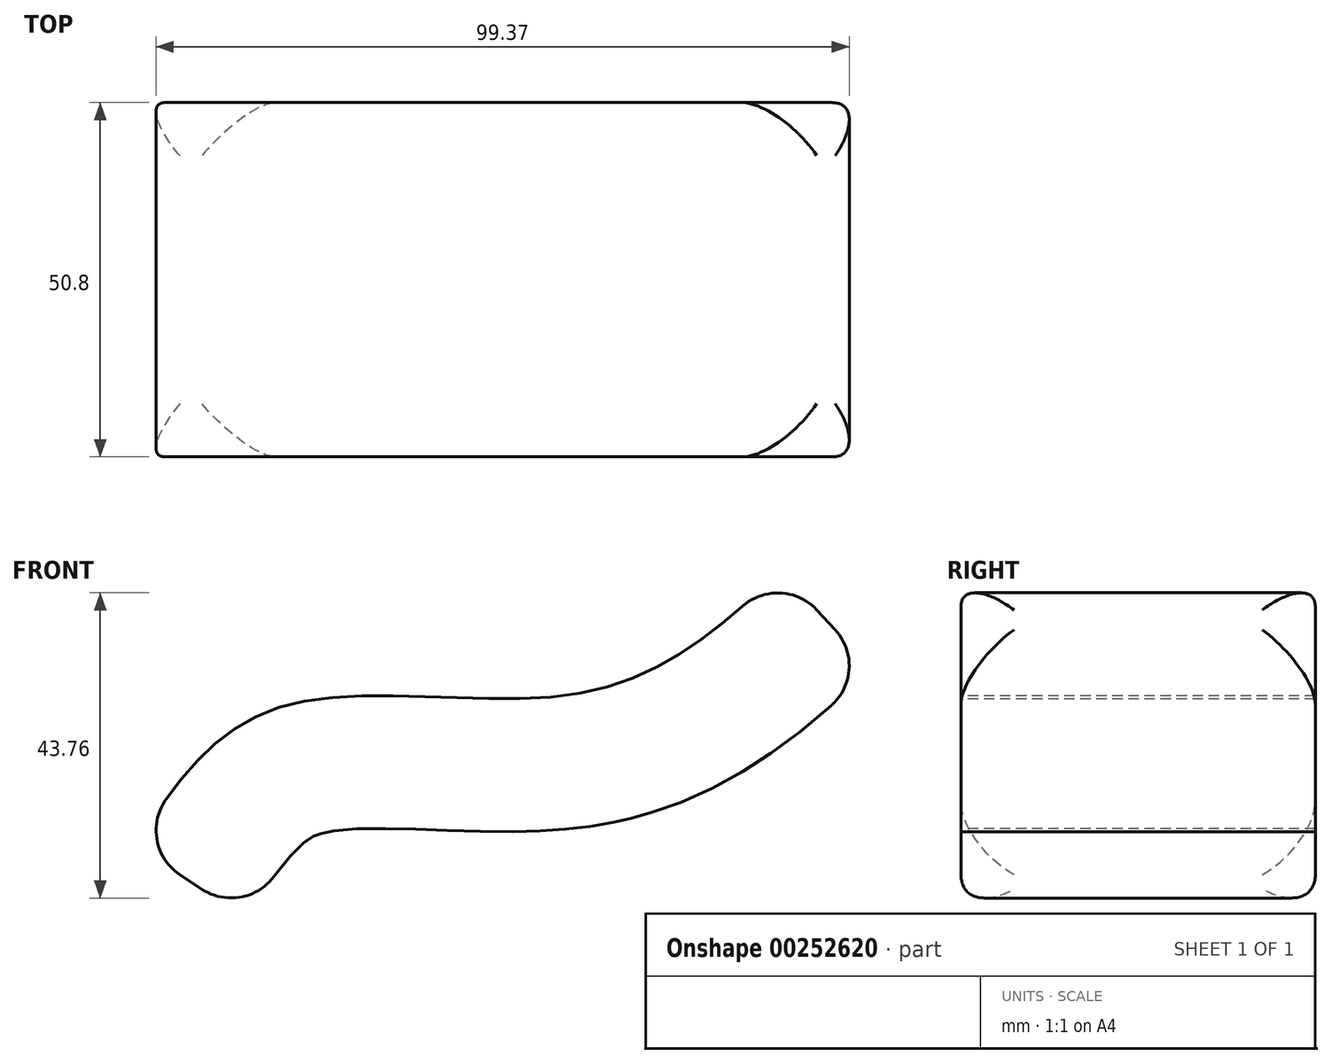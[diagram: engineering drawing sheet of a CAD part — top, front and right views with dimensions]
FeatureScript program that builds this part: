
annotation { "Feature Type Name" : "Feature", "Feature Type Description" : "" }
export const myFeature = defineFeature(function(context is Context, id is Id, definition is map)
    precondition{}
    {
        {
            var Q0;
            Q0=qCreatedBy(makeId("Front.planeOp"),FACE);
            var sketch = newSketch(context, id + "F0", { "sketchPlane" : qUnion([Q0])});
            skFitSpline(sketch, "E0", {"points": [v(-51.04, 0) * mm, v(-30.35, 19.7) * mm, v(13.6, 21.87) * mm, v(41.58, 39.22) * mm], "startDerivative": vector(54.82, 82.75) * mm, "endDerivative": vector(75.26, 69.64) * mm});
            skFitSpline(sketch, "E1.0", {"points": [v(-35.16, -10.52) * mm, v(-34.02, -8.8) * mm, v(-32.44, -6.43) * mm, v(-30.57, -3.84) * mm, v(-29.28, -2.22) * mm, v(-28.12, -0.93) * mm, v(-27.12, 0.03) * mm, v(-26.43, 0.58) * mm, v(-25.95, 0.9) * mm, v(-25.62, 1.1) * mm, v(-25.31, 1.26) * mm, v(-25.02, 1.4) * mm, v(-24.75, 1.5) * mm, v(-24.53, 1.57) * mm, v(-24.32, 1.63) * mm, v(-24.07, 1.7) * mm, v(-23.66, 1.79) * mm, v(-22.8, 1.95) * mm, v(-21.12, 2.16) * mm, v(-18.55, 2.3) * mm, v(-15.5, 2.33) * mm, v(-12.06, 2.26) * mm, v(-8.3, 2.13) * mm, v(-4.28, 1.99) * mm, v(-0.02, 1.88) * mm, v(3.7, 1.89) * mm, v(6.78, 1.99) * mm, v(9.14, 2.12) * mm, v(11.56, 2.33) * mm, v(14.03, 2.62) * mm, v(16.14, 2.96) * mm, v(17.86, 3.3) * mm, v(19.13, 3.58) * mm, v(20.38, 3.88) * mm, v(22.03, 4.33) * mm, v(24.85, 5.19) * mm, v(28.68, 6.65) * mm, v(32.93, 8.7) * mm, v(36.84, 10.95) * mm, v(40.42, 13.33) * mm, v(44.8, 16.6) * mm, v(49.62, 20.7) * mm, v(52.95, 23.78) * mm, v(54.52, 25.23) * mm]});
            skLineSegment(sketch, "E2", {"start": v(-51.04, 0) * mm, "end": v(-35.16, -10.52) * mm});
            skLineSegment(sketch, "E3", {"start": v(41.58, 39.22) * mm, "end": v(54.52, 25.23) * mm});
            skSolve(sketch);
        }
        {
            var Q0;
            Q0 = qSketchRegion(id + "F0", true);
            extrude(context, id + "F1", {"entities" : qUnion([Q0]), "depth" : 50.8 * mm});
        }
        {
            var Q0;
            Q0=makeQuery(id+"F1.opExtrude","SWEPT_FACE",FACE,{"disambiguationData":[OSD([sQuery(id+"F0.wireOp",EDGE,"E3")])]});
            var Q1;
            Q1=makeQuery(id+"F1.opExtrude","SWEPT_FACE",FACE,{"disambiguationData":[OSD([sQuery(id+"F0.wireOp",EDGE,"E2")])]});
            fillet(context, id + "F2", {"entities" : qUnion([Q0, Q1]), "radius" : 7.62 * mm, "tangentPropagation" : true, "allowEdgeOverflow" : false});
        }
    });
